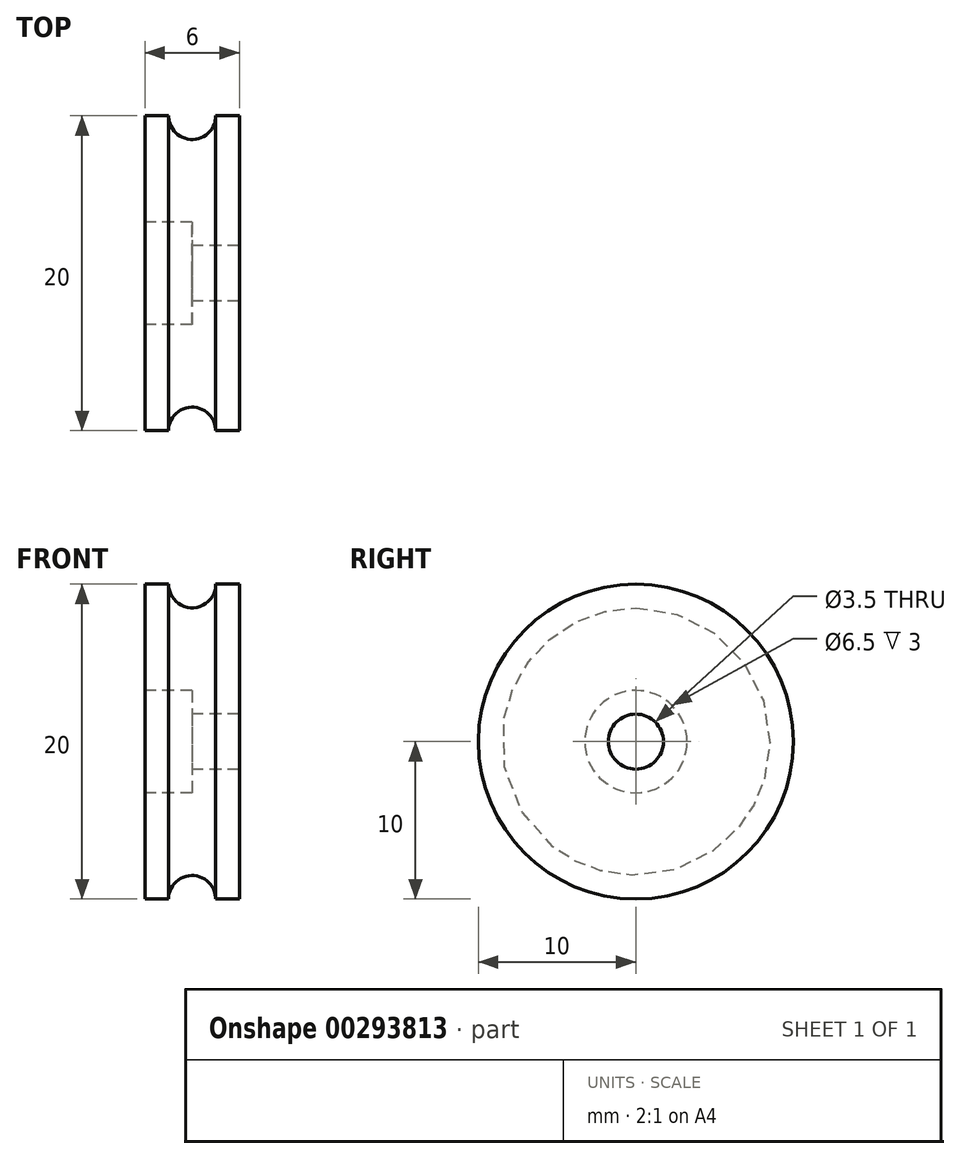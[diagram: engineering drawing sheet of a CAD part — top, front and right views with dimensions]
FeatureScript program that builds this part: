
annotation { "Feature Type Name" : "Feature", "Feature Type Description" : "" }
export const myFeature = defineFeature(function(context is Context, id is Id, definition is map)
    precondition{}
    {
        {
            var Q0;
            Q0=qCreatedBy(makeId("Top.planeOp"),FACE);
            var sketch = newSketch(context, id + "F0", { "sketchPlane" : qUnion([Q0])});
            skLineSegment(sketch, "E0", {"start": v(3, 0) * mm, "end": v(3, 10) * mm});
            skLineSegment(sketch, "E1", {"start": v(-3, 0) * mm, "end": v(-3, 10) * mm});
            skLineSegment(sketch, "E2", {"start": v(-3, 0) * mm, "end": v(3, 0) * mm});
            skLineSegment(sketch, "E3", {"start": v(-3, 10) * mm, "end": v(-1.5, 10) * mm});
            skLineSegment(sketch, "E4", {"start": v(3, 10) * mm, "end": v(1.5, 10) * mm});
            skArc(sketch, "E5", {"start": v(-1.5, 10) * mm, "mid": v(0, 8.5) * mm, "end": v(1.5, 10) * mm});
            skSolve(sketch);
        }
        {
            var Q0;
            Q0 = qSketchRegion(id + "F0", true);
            var Q1;
            Q1=sQuery(id+"F0.wireOp",EDGE,"E2");
            revolve(context, id + "F1", {"entities" : qUnion([Q0]), "axis" : qUnion([Q1]), "revolveType" : RevolveType.FULL});
        }
        {
            var Q0;
            Q0=makeQuery(id+"F1.opRevolve","SWEPT_FACE",FACE,{"disambiguationData":[OSD([sQuery(id+"F0.wireOp",EDGE,"E1")])]});
            cPlane(context, id + "F2", {"entities" : qUnion([Q0]), "cplaneType" : CPlaneType.OFFSET, "offset" : 0 * mm, "width" : 150 * mm, "height" : 150 * mm});
        }
        {
            var Q0;
            Q0=qCreatedBy(id+"F2.planeOp",FACE);
            var sketch = newSketch(context, id + "F3", { "sketchPlane" : qUnion([Q0])});
            skCircle(sketch, "E6", {"center": v(0, 0) * mm, "radius": 1.75 * mm});
            skSolve(sketch);
        }
        {
            var Q0;
            Q0 = qSketchRegion(id + "F3", true);
            var Q1;
            Q1=makeQuery(id+"F1.opRevolve","SWEPT_FACE",FACE,{"disambiguationData":[OSD([sQuery(id+"F0.wireOp",EDGE,"E0")])]});
            extrude(context, id + "F4", {"entities" : qUnion([Q0]), "operationType" : NewBodyOperationType.REMOVE, "endBound" : BoundingType.UP_TO_SURFACE, "oppositeDirection" : true, "endBoundEntityFace" : qUnion([Q1]), "depth" : 25 * mm});
        }
        {
            var Q0;
            Q0=qCreatedBy(id+"F2.planeOp",FACE);
            var sketch = newSketch(context, id + "F5", { "sketchPlane" : qUnion([Q0])});
            skCircle(sketch, "E7", {"center": v(0, 0) * mm, "radius": 3.25 * mm});
            skSolve(sketch);
        }
        {
            var Q0;
            Q0 = qSketchRegion(id + "F5", true);
            extrude(context, id + "F6", {"entities" : qUnion([Q0]), "operationType" : NewBodyOperationType.REMOVE, "oppositeDirection" : true, "depth" : 3 * mm});
        }
    });
